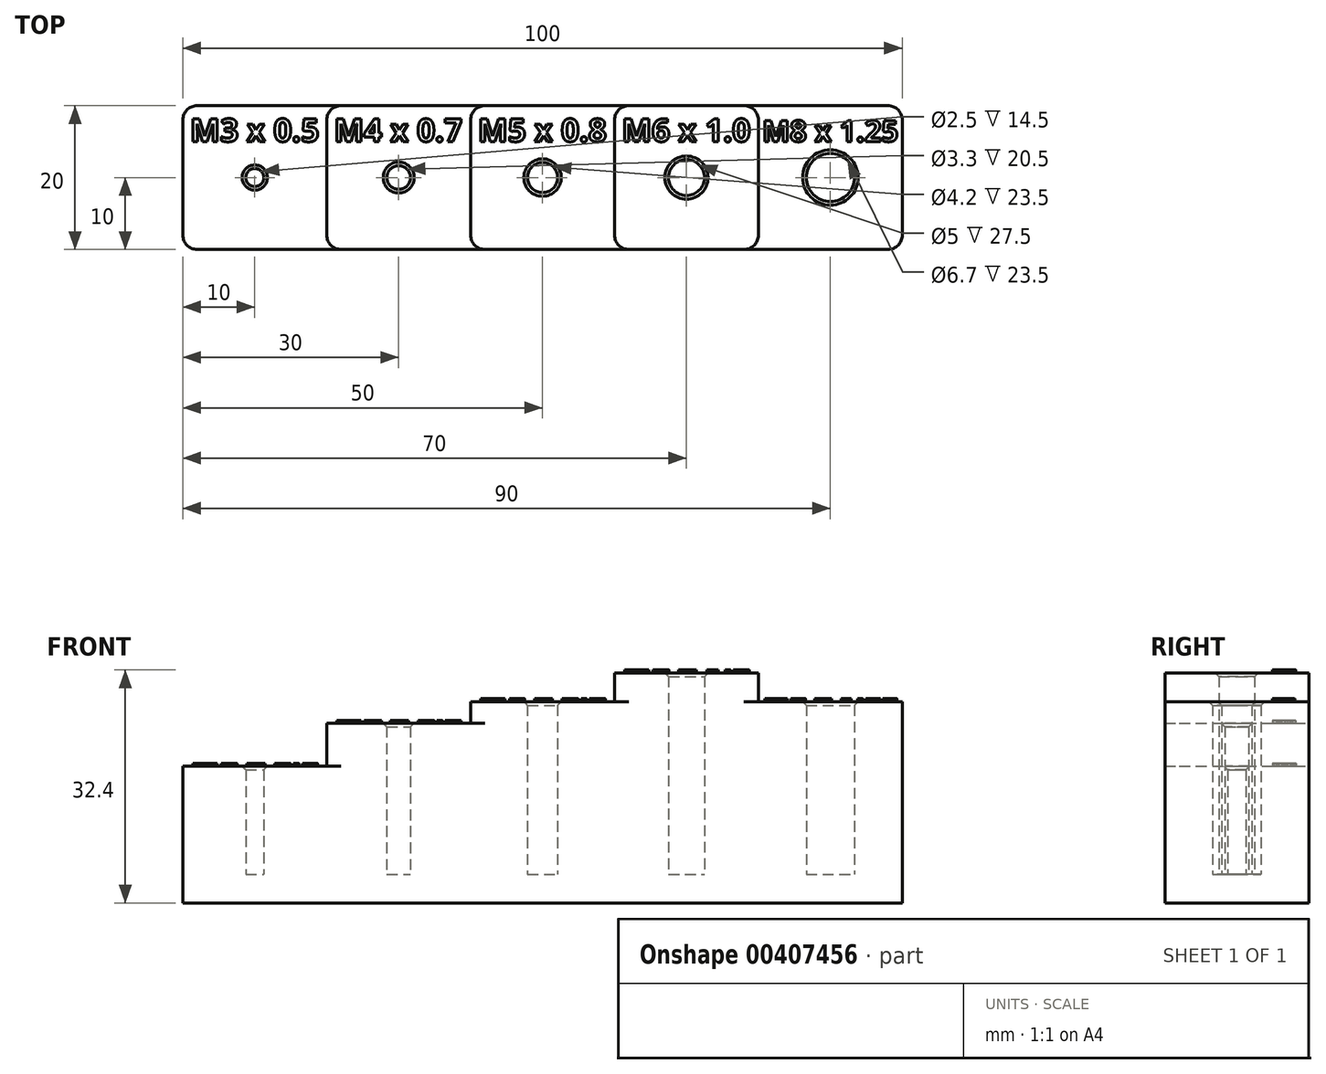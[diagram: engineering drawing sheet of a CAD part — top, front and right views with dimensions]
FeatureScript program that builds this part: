
annotation { "Feature Type Name" : "Feature", "Feature Type Description" : "" }
export const myFeature = defineFeature(function(context is Context, id is Id, definition is map)
    precondition{}
    {
        {
            var Q0;
            Q0=qCreatedBy(makeId("Front.planeOp"),FACE);
            var sketch = newSketch(context, id + "F0", { "sketchPlane" : qUnion([Q0])});
            skLineSegment(sketch, "E0", {"start": v(0, 0) * mm, "end": v(100, 0) * mm});
            skLineSegment(sketch, "E1", {"start": v(100, 0) * mm, "end": v(100, 28) * mm});
            skLineSegment(sketch, "E2", {"start": v(100, 28) * mm, "end": v(80, 28) * mm});
            skLineSegment(sketch, "E3", {"start": v(80, 32) * mm, "end": v(80, 28) * mm});
            skLineSegment(sketch, "E4", {"start": v(80, 32) * mm, "end": v(60, 32) * mm});
            skLineSegment(sketch, "E5", {"start": v(60, 32) * mm, "end": v(60, 28) * mm});
            skLineSegment(sketch, "E6", {"start": v(60, 28) * mm, "end": v(40, 28) * mm});
            skLineSegment(sketch, "E7", {"start": v(40, 28) * mm, "end": v(40, 25) * mm});
            skLineSegment(sketch, "E8", {"start": v(40, 25) * mm, "end": v(20, 25) * mm});
            skLineSegment(sketch, "E9", {"start": v(20, 25) * mm, "end": v(20, 19) * mm});
            skLineSegment(sketch, "E10", {"start": v(20, 19) * mm, "end": v(0, 19) * mm});
            skLineSegment(sketch, "E11", {"start": v(0, 19) * mm, "end": v(0, 0) * mm});
            skSolve(sketch);
        }
        {
            var Q0;
            Q0 = qSketchRegion(id + "F0", true);
            extrude(context, id + "F1", {"entities" : qUnion([Q0]), "depth" : 20 * mm});
        }
        {
            var Q0;
            Q0=makeQuery(id+"F1.opExtrude","SWEPT_FACE",FACE,{"disambiguationData":[OSD([sQuery(id+"F0.wireOp",EDGE,"E0")])]});
            cPlane(context, id + "F2", {"entities" : qUnion([Q0]), "cplaneType" : CPlaneType.OFFSET, "offset" : 4 * mm, "oppositeDirection" : true, "width" : 150 * mm, "height" : 150 * mm});
        }
        {
            var Q0;
            Q0=qCreatedBy(id+"F2.planeOp",FACE);
            var sketch = newSketch(context, id + "F3", { "sketchPlane" : qUnion([Q0])});
            skLineSegment(sketch, "E12", {"start": v(0, 10) * mm, "end": v(100, 10) * mm, "construction": true});
            skLineSegment(sketch, "E13", {"start": v(10, 0) * mm, "end": v(10, 19.98) * mm, "construction": true});
            skLineSegment(sketch, "E14", {"start": v(30, 0) * mm, "end": v(30, 20) * mm, "construction": true});
            skLineSegment(sketch, "E15", {"start": v(50, 0) * mm, "end": v(50, 20.06) * mm, "construction": true});
            skLineSegment(sketch, "E16", {"start": v(70, 0) * mm, "end": v(70, 20) * mm, "construction": true});
            skLineSegment(sketch, "E17", {"start": v(90, 0) * mm, "end": v(90, 19.98) * mm, "construction": true});
            skCircle(sketch, "E18", {"center": v(10, 10) * mm, "radius": 1.25 * mm});
            skCircle(sketch, "E19", {"center": v(30, 10) * mm, "radius": 1.65 * mm});
            skPoint(sketch, "E19.centerSnap0", {"position": v(30, 10) * mm});
            skCircle(sketch, "E20", {"center": v(50, 10) * mm, "radius": 2.1 * mm});
            skCircle(sketch, "E21", {"center": v(70, 10) * mm, "radius": 2.5 * mm});
            skCircle(sketch, "E22", {"center": v(90, 10) * mm, "radius": 3.35 * mm});
            skSolve(sketch);
        }
        {
            var Q0;
            Q0 = qSketchRegion(id + "F3", true);
            extrude(context, id + "F4", {"entities" : qUnion([Q0]), "operationType" : NewBodyOperationType.REMOVE, "endBound" : BoundingType.THROUGH_ALL, "oppositeDirection" : true, "depth" : 25 * mm});
        }
        {
            var Q0;
            Q0=makeQuery(id+"F1.opExtrude","SWEPT_FACE",FACE,{"disambiguationData":[OSD([sQuery(id+"F0.wireOp",EDGE,"E10")])]});
            var sketch = newSketch(context, id + "F5", { "sketchPlane" : qUnion([Q0])});
            skText(sketch, "E23", { "text": "M3 x 0.5", "fontName": "OpenSans-Bold.ttf"});
            const initialGuessF5  = {"E23": [0.001, -0.005, 1, 0, 0.0032]};
            skSetInitialGuess(sketch, initialGuessF5);
            skSolve(sketch);
        }
        {
            var Q0;
            Q0 = qSketchRegion(id + "F5", true);
            extrude(context, id + "F6", {"entities" : qUnion([Q0]), "operationType" : NewBodyOperationType.ADD, "depth" : .4 * mm});
        }
        {
            var Q0;
            Q0=makeQuery(id+"F1.opExtrude","SWEPT_FACE",FACE,{"disambiguationData":[OSD([sQuery(id+"F0.wireOp",EDGE,"E8")])]});
            var sketch = newSketch(context, id + "F7", { "sketchPlane" : qUnion([Q0])});
            skText(sketch, "E24", { "text": "M4 x 0.7", "fontName": "OpenSans-Bold.ttf"});
            const initialGuessF7  = {"E24": [0.021, -0.005, 1, 0, 0.00318]};
            skSetInitialGuess(sketch, initialGuessF7);
            skSolve(sketch);
        }
        {
            var Q0;
            Q0 = qSketchRegion(id + "F7", true);
            extrude(context, id + "F8", {"entities" : qUnion([Q0]), "operationType" : NewBodyOperationType.ADD, "depth" : .4 * mm});
        }
        {
            var Q0;
            Q0=makeQuery(id+"F1.opExtrude","SWEPT_FACE",FACE,{"disambiguationData":[OSD([sQuery(id+"F0.wireOp",EDGE,"E6")])]});
            var sketch = newSketch(context, id + "F9", { "sketchPlane" : qUnion([Q0])});
            skText(sketch, "E25", { "text": "M5 x 0.8", "fontName": "OpenSans-Bold.ttf"});
            const initialGuessF9  = {"E25": [0.041, -0.005, 1, 0, 0.00319]};
            skSetInitialGuess(sketch, initialGuessF9);
            skSolve(sketch);
        }
        {
            var Q0;
            Q0 = qSketchRegion(id + "F9", true);
            extrude(context, id + "F10", {"entities" : qUnion([Q0]), "operationType" : NewBodyOperationType.ADD, "depth" : .4 * mm});
        }
        {
            var Q0;
            Q0=makeQuery(id+"F1.opExtrude","SWEPT_FACE",FACE,{"disambiguationData":[OSD([sQuery(id+"F0.wireOp",EDGE,"E4")])]});
            var sketch = newSketch(context, id + "F11", { "sketchPlane" : qUnion([Q0])});
            skText(sketch, "E26", { "text": "M6 x 1.0", "fontName": "OpenSans-Bold.ttf"});
            const initialGuessF11  = {"E26": [0.061, -0.005, 1, 0, 0.00319]};
            skSetInitialGuess(sketch, initialGuessF11);
            skSolve(sketch);
        }
        {
            var Q0;
            Q0 = qSketchRegion(id + "F11", true);
            extrude(context, id + "F12", {"entities" : qUnion([Q0]), "operationType" : NewBodyOperationType.ADD, "depth" : .4 * mm});
        }
        {
            var Q0;
            Q0=makeQuery(id+"F1.opExtrude","SWEPT_FACE",FACE,{"disambiguationData":[OSD([sQuery(id+"F0.wireOp",EDGE,"E2")])]});
            var sketch = newSketch(context, id + "F13", { "sketchPlane" : qUnion([Q0])});
            skText(sketch, "E27", { "text": "M8 x 1.25", "fontName": "OpenSans-Bold.ttf"});
            const initialGuessF13  = {"E27": [0.0805, -0.005, 1, 0, 0.00296]};
            skSetInitialGuess(sketch, initialGuessF13);
            skSolve(sketch);
        }
        {
            var Q0;
            Q0 = qSketchRegion(id + "F13", true);
            extrude(context, id + "F14", {"entities" : qUnion([Q0]), "operationType" : NewBodyOperationType.ADD, "depth" : .4 * mm});
        }
        {
            var Q0;
            Q0=makeQuery(id+"F4.boolean.opBoolean","INTERSECT",EDGE,{"derivedFrom":[makeQuery(id+"F1.opExtrude","SWEPT_FACE",FACE,{"disambiguationData":[OSD([sQuery(id+"F0.wireOp",EDGE,"E10")])]}),makeQuery(id+"F4.opExtrude","SWEPT_FACE",FACE,{"disambiguationData":[OSD([sQuery(id+"F3.wireOp",EDGE,"E18")])]})]});
            var Q1;
            Q1=makeQuery(id+"F4.boolean.opBoolean","INTERSECT",EDGE,{"derivedFrom":[makeQuery(id+"F1.opExtrude","SWEPT_FACE",FACE,{"disambiguationData":[OSD([sQuery(id+"F0.wireOp",EDGE,"E8")])]}),makeQuery(id+"F4.opExtrude","SWEPT_FACE",FACE,{"disambiguationData":[OSD([sQuery(id+"F3.wireOp",EDGE,"E19")])]})]});
            var Q2;
            Q2=makeQuery(id+"F4.boolean.opBoolean","INTERSECT",EDGE,{"derivedFrom":[makeQuery(id+"F1.opExtrude","SWEPT_FACE",FACE,{"disambiguationData":[OSD([sQuery(id+"F0.wireOp",EDGE,"E6")])]}),makeQuery(id+"F4.opExtrude","SWEPT_FACE",FACE,{"disambiguationData":[OSD([sQuery(id+"F3.wireOp",EDGE,"E20")])]})]});
            var Q3;
            Q3=makeQuery(id+"F4.boolean.opBoolean","INTERSECT",EDGE,{"derivedFrom":[makeQuery(id+"F1.opExtrude","SWEPT_FACE",FACE,{"disambiguationData":[OSD([sQuery(id+"F0.wireOp",EDGE,"E4")])]}),makeQuery(id+"F4.opExtrude","SWEPT_FACE",FACE,{"disambiguationData":[OSD([sQuery(id+"F3.wireOp",EDGE,"E21")])]})]});
            var Q4;
            Q4=makeQuery(id+"F4.boolean.opBoolean","INTERSECT",EDGE,{"derivedFrom":[makeQuery(id+"F1.opExtrude","SWEPT_FACE",FACE,{"disambiguationData":[OSD([sQuery(id+"F0.wireOp",EDGE,"E2")])]}),makeQuery(id+"F4.opExtrude","SWEPT_FACE",FACE,{"disambiguationData":[OSD([sQuery(id+"F3.wireOp",EDGE,"E22")])]})]});
            chamfer(context, id + "F15", {"entities" : qUnion([Q0, Q1, Q2, Q3, Q4]), "width" : .5 * mm, "tangentPropagation" : true});
        }
        {
            var Q0;
            Q0=makeQuery(id+"F1.opExtrude","CAP_EDGE",EDGE,{"disambiguationData":[OSD([sQuery(id+"F0.wireOp",EDGE,"E11")])],"isStart":false});
            var Q1;
            Q1=makeQuery(id+"F1.opExtrude","CAP_EDGE",EDGE,{"disambiguationData":[OSD([sQuery(id+"F0.wireOp",EDGE,"E11")])],"isStart":true});
            var Q2;
            Q2=makeQuery(id+"F1.opExtrude","CAP_EDGE",EDGE,{"disambiguationData":[OSD([sQuery(id+"F0.wireOp",EDGE,"E9")])],"isStart":false});
            var Q3;
            Q3=makeQuery(id+"F1.opExtrude","CAP_EDGE",EDGE,{"disambiguationData":[OSD([sQuery(id+"F0.wireOp",EDGE,"E9")])],"isStart":true});
            var Q4;
            Q4=makeQuery(id+"F1.opExtrude","CAP_EDGE",EDGE,{"disambiguationData":[OSD([sQuery(id+"F0.wireOp",EDGE,"E7")])],"isStart":true});
            var Q5;
            Q5=makeQuery(id+"F1.opExtrude","CAP_EDGE",EDGE,{"disambiguationData":[OSD([sQuery(id+"F0.wireOp",EDGE,"E7")])],"isStart":false});
            var Q6;
            Q6=makeQuery(id+"F1.opExtrude","CAP_EDGE",EDGE,{"disambiguationData":[OSD([sQuery(id+"F0.wireOp",EDGE,"E5")])],"isStart":false});
            var Q7;
            Q7=makeQuery(id+"F1.opExtrude","CAP_EDGE",EDGE,{"disambiguationData":[OSD([sQuery(id+"F0.wireOp",EDGE,"E5")])],"isStart":true});
            var Q8;
            Q8=makeQuery(id+"F1.opExtrude","CAP_EDGE",EDGE,{"disambiguationData":[OSD([sQuery(id+"F0.wireOp",EDGE,"E3")])],"isStart":false});
            var Q9;
            Q9=makeQuery(id+"F1.opExtrude","CAP_EDGE",EDGE,{"disambiguationData":[OSD([sQuery(id+"F0.wireOp",EDGE,"E3")])],"isStart":true});
            var Q10;
            Q10=makeQuery(id+"F1.opExtrude","CAP_EDGE",EDGE,{"disambiguationData":[OSD([sQuery(id+"F0.wireOp",EDGE,"E1")])],"isStart":true});
            var Q11;
            Q11=makeQuery(id+"F1.opExtrude","CAP_EDGE",EDGE,{"disambiguationData":[OSD([sQuery(id+"F0.wireOp",EDGE,"E1")])],"isStart":false});
            fillet(context, id + "F16", {"entities" : qUnion([Q0, Q1, Q2, Q3, Q4, Q5, Q6, Q7, Q8, Q9, Q10, Q11]), "radius" : 2 * mm, "tangentPropagation" : true, "allowEdgeOverflow" : false});
        }
    });
